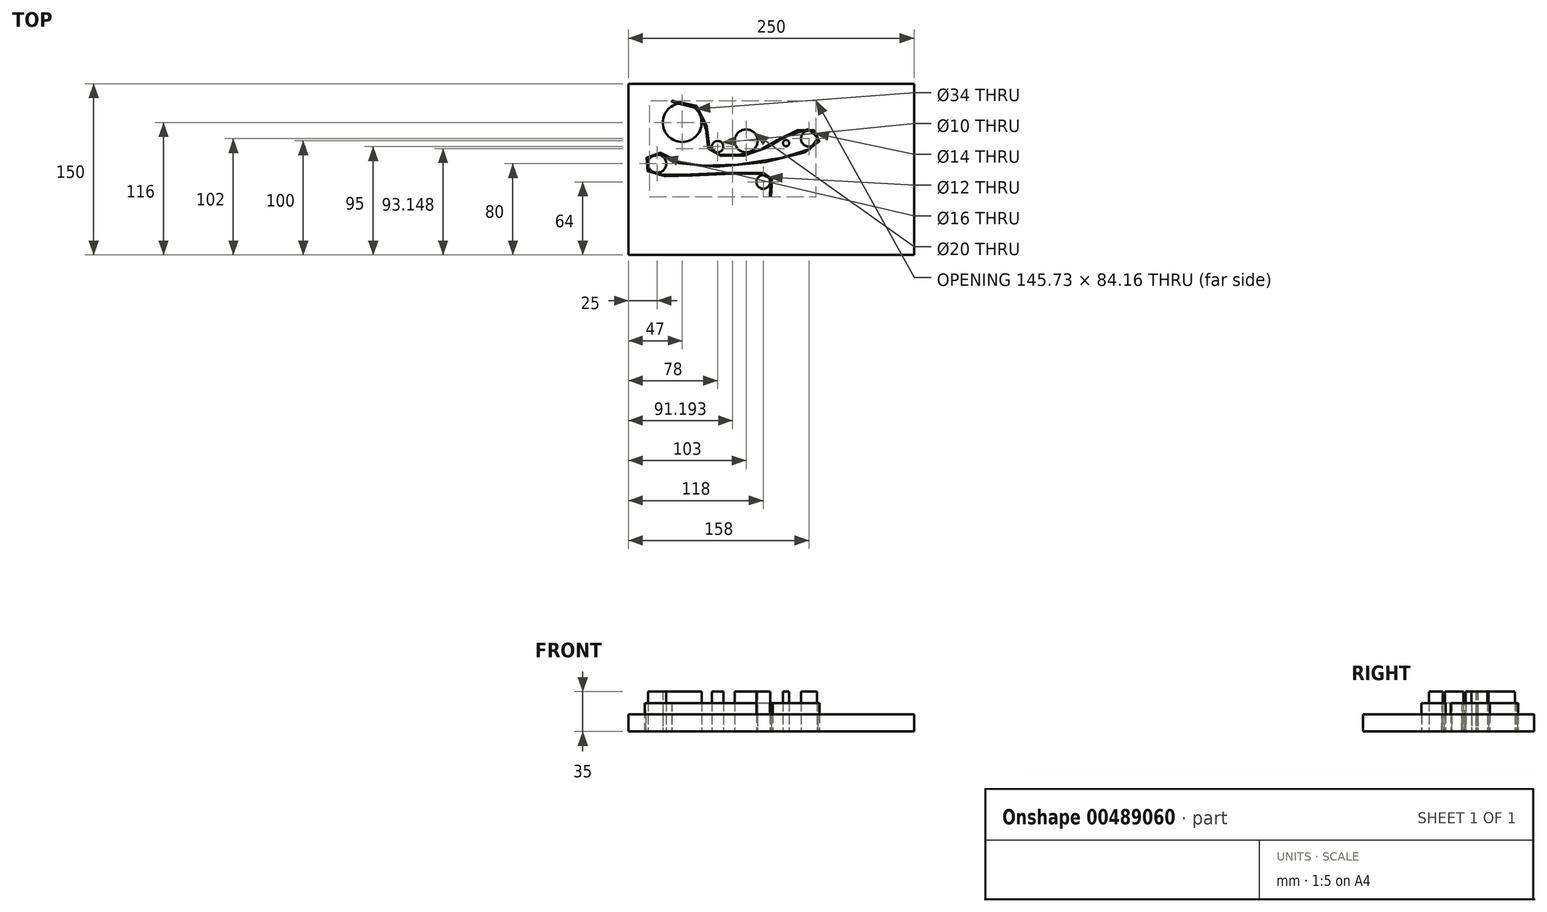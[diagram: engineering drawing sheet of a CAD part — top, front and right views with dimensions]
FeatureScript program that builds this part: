
annotation { "Feature Type Name" : "Feature", "Feature Type Description" : "" }
export const myFeature = defineFeature(function(context is Context, id is Id, definition is map)
    precondition{}
    {
        {
            var Q0;
            Q0=qCreatedBy(makeId("Top.planeOp"),FACE);
            var sketch = newSketch(context, id + "F0", { "sketchPlane" : qUnion([Q0])});
            skLineSegment(sketch, "E0.bottom", {"start": v(-113, 112) * mm, "end": v(137, 112) * mm});
            skLineSegment(sketch, "E0.top", {"start": v(-113, -38) * mm, "end": v(137, -38) * mm});
            skLineSegment(sketch, "E0.left", {"start": v(-113, 112) * mm, "end": v(-113, -38) * mm});
            skLineSegment(sketch, "E0.right", {"start": v(137, 112) * mm, "end": v(137, -38) * mm});
            skCircle(sketch, "E1", {"center": v(-66, 78) * mm, "radius": 17 * mm});
            skCircle(sketch, "E2", {"center": v(-35, 57) * mm, "radius": 5 * mm});
            skCircle(sketch, "E3", {"center": v(-10, 62) * mm, "radius": 10 * mm});
            skCircle(sketch, "E4", {"center": v(45, 64) * mm, "radius": 7 * mm});
            skCircle(sketch, "E5", {"center": v(25, 60) * mm, "radius": 2.75 * mm});
            skCircle(sketch, "E6", {"center": v(5, 26) * mm, "radius": 6 * mm});
            skCircle(sketch, "E7", {"center": v(-88, 42) * mm, "radius": 8 * mm});
            skLineSegment(sketch, "E8", {"start": v(-35, 62) * mm, "end": v(-14, 71.17) * mm});
            skLineSegment(sketch, "E9", {"start": v(-35, 52) * mm, "end": v(-10, 52) * mm});
            skFitSpline(sketch, "E10", {"points": [v(-75.22, 97.23) * mm, v(-45.88, 80.85) * mm, v(-41.4, 53.92) * mm, v(-30.29, 49.78) * mm, v(-3.76, 51.88) * mm, v(21.1, 64.78) * mm, v(47.28, 72.74) * mm, v(53.96, 64.44) * mm, v(47.46, 54.45) * mm, v(-64.37, 41.14) * mm, v(-88.04, 51.12) * mm, v(-97.25, 44.82) * mm, v(-95.52, 36.29) * mm, v(-81.1, 32.03) * mm, v(4.23, 34.03) * mm, v(12.06, 30.05) * mm, v(11.61, 13.07) * mm], "startDerivative": vector(662.98, 157.54) * mm, "endDerivative": vector(-153.55, -571.99) * mm});
            skFitSpline(sketch, "E11.0", {"points": [v(-75, 96.25) * mm, v(-71.63, 97.05) * mm, v(-65.54, 97.5) * mm, v(-58.23, 95.4) * mm, v(-53.51, 91.88) * mm, v(-50.52, 88.26) * mm, v(-48.68, 85.2) * mm, v(-47.23, 81.9) * mm, v(-46.18, 78.42) * mm, v(-45.47, 74.82) * mm, v(-45, 71.18) * mm, v(-44.7, 67.6) * mm, v(-44.47, 64.13) * mm, v(-44.2, 60.88) * mm, v(-43.87, 58.4) * mm, v(-43.49, 56.59) * mm, v(-43.13, 55.32) * mm, v(-42.67, 54.15) * mm, v(-42.1, 53.1) * mm, v(-41.4, 52.17) * mm, v(-40.31, 51.13) * mm, v(-38.72, 50.17) * mm, v(-36.55, 49.47) * mm, v(-34.15, 49.06) * mm, v(-31.98, 48.88) * mm, v(-30.15, 48.77) * mm, v(-28.24, 48.68) * mm, v(-25.74, 48.59) * mm, v(-21.53, 48.54) * mm, v(-15.98, 48.72) * mm, v(-10.35, 49.35) * mm, v(-5.96, 50.23) * mm, v(-2.76, 51.1) * mm, v(0.28, 52.18) * mm, v(4.2, 53.87) * mm, v(8.89, 56.37) * mm, v(13.57, 59.19) * mm, v(17.45, 61.52) * mm, v(19.97, 63) * mm, v(22.05, 64.17) * mm, v(24.19, 65.33) * mm, v(26.93, 66.75) * mm, v(30.28, 68.33) * mm, v(34.71, 70.19) * mm, v(38.98, 71.54) * mm, v(42.77, 72.14) * mm, v(44.87, 72.17) * mm, v(46.35, 71.96) * mm, v(47.35, 71.69) * mm, v(48.26, 71.3) * mm, v(49.36, 70.64) * mm, v(50.55, 69.58) * mm, v(51.67, 68) * mm, v(52.35, 66.55) * mm, v(52.74, 65.35) * mm, v(52.95, 64.45) * mm, v(53.09, 63.58) * mm, v(53.15, 62.46) * mm, v(53, 61.16) * mm, v(52.36, 59.66) * mm, v(51.13, 58.1) * mm, v(49.44, 56.76) * mm, v(47.64, 55.67) * mm, v(45.52, 54.56) * mm, v(42.26, 53.15) * mm, v(37.5, 51.47) * mm, v(32.01, 49.83) * mm, v(23.86, 47.73) * mm, v(12.34, 45.3) * mm, v(-2.78, 42.85) * mm, v(-18.38, 41.05) * mm, v(-31.13, 40.22) * mm, v(-40.76, 40.02) * mm, v(-47.6, 40.13) * mm, v(-53.97, 40.52) * mm, v(-58.77, 41.09) * mm, v(-62.27, 41.7) * mm, v(-64.7, 42.23) * mm, v(-66.95, 42.84) * mm, v(-69.7, 43.74) * mm, v(-72.76, 45) * mm, v(-75.9, 46.6) * mm, v(-78.62, 48.18) * mm, v(-81.04, 49.65) * mm, v(-83.3, 50.9) * mm, v(-85.13, 51.66) * mm, v(-86.64, 52.02) * mm, v(-87.8, 52.15) * mm, v(-89, 52.1) * mm, v(-90.57, 51.82) * mm, v(-92.47, 51.13) * mm, v(-94.57, 49.84) * mm, v(-96.08, 48.47) * mm, v(-97.08, 47.24) * mm, v(-97.7, 46.25) * mm, v(-98.2, 45.2) * mm, v(-98.53, 44.11) * mm, v(-98.7, 43.02) * mm, v(-98.74, 41.57) * mm, v(-98.47, 39.8) * mm, v(-97.73, 37.83) * mm, v(-96.68, 36.07) * mm, v(-95.4, 34.58) * mm, v(-93.84, 33.37) * mm, v(-91.93, 32.45) * mm, v(-89.63, 31.79) * mm, v(-86.83, 31.35) * mm, v(-84.02, 31.13) * mm, v(-81.42, 31.04) * mm, v(-78.57, 30.98) * mm, v(-74.57, 31) * mm, v(-69.16, 31.12) * mm, v(-63.27, 31.33) * mm, v(-54.89, 31.69) * mm, v(-43.73, 32.24) * mm, v(-30.14, 32.92) * mm, v(-19.38, 33.35) * mm, v(-11.57, 33.53) * mm, v(-6.22, 33.56) * mm, v(-2.27, 33.5) * mm, v(0.5, 33.36) * mm, v(2.4, 33.23) * mm, v(4.06, 33.06) * mm, v(5.5, 32.84) * mm, v(6.7, 32.6) * mm, v(8.06, 32.2) * mm, v(9.3, 31.65) * mm, v(10.11, 31.01) * mm, v(10.63, 30.42) * mm, v(10.97, 29.93) * mm, v(11.3, 29.36) * mm, v(11.6, 28.75) * mm, v(11.85, 28.1) * mm, v(12.14, 27.12) * mm, v(12.4, 25.68) * mm, v(12.47, 23.52) * mm, v(12.18, 19.91) * mm, v(11.44, 16.28) * mm, v(10.65, 13.33) * mm]});
            skLineSegment(sketch, "E12", {"start": v(-75.22, 97.23) * mm, "end": v(-75, 96.25) * mm});
            skLineSegment(sketch, "E13", {"start": v(11.61, 13.07) * mm, "end": v(10.69, 13.49) * mm});
            skSolve(sketch);
        }
        {
            var Q0;
            Q0=makeQuery(id+"F0.imprint","IMPRINT",FACE,{"disambiguationData":[TD([[makeQuery(id+"F0.imprint","IMPRINT",EDGE,{"derivedFrom":sQuery(id+"F0.wireOp",EDGE,"E7")}),1.0]])]});
            var Q1;
            Q1=makeQuery(id+"F0.imprint","IMPRINT",FACE,{"disambiguationData":[TD([[makeQuery(id+"F0.imprint","IMPRINT",EDGE,{"derivedFrom":sQuery(id+"F0.wireOp",EDGE,"E1")}),1.0]])]});
            var Q2;
            {var subQ0=sQuery(id+"F0.wireOp",EDGE,"E2");var subQ1=makeQuery(id+"F0.imprint","INTERSECT",VERTEX,{"derivedFrom":[subQ0,sQuery(id+"F0.wireOp",EDGE,"E8")]});Q2=makeQuery(id+"F0.imprint","IMPRINT",FACE,{"disambiguationData":[TD([[makeQuery(id+"F0.imprint","IMPRINT",EDGE,{"disambiguationData":[TD([[subQ1,-1.0]])],"derivedFrom":subQ0}),1.0]])]});}
            var Q3;
            {var subQ0=sQuery(id+"F0.wireOp",EDGE,"E3");var subQ1=makeQuery(id+"F0.imprint","INTERSECT",VERTEX,{"derivedFrom":[subQ0,sQuery(id+"F0.wireOp",EDGE,"E8")]});Q3=makeQuery(id+"F0.imprint","IMPRINT",FACE,{"disambiguationData":[TD([[makeQuery(id+"F0.imprint","IMPRINT",EDGE,{"disambiguationData":[TD([[subQ1,-1.0]])],"derivedFrom":subQ0}),1.0]])]});}
            var Q4;
            Q4=makeQuery(id+"F0.imprint","IMPRINT",FACE,{"disambiguationData":[TD([[makeQuery(id+"F0.imprint","IMPRINT",EDGE,{"derivedFrom":sQuery(id+"F0.wireOp",EDGE,"E6")}),1.0]])]});
            var Q5;
            Q5=makeQuery(id+"F0.imprint","IMPRINT",FACE,{"disambiguationData":[TD([[makeQuery(id+"F0.imprint","IMPRINT",EDGE,{"derivedFrom":sQuery(id+"F0.wireOp",EDGE,"E4")}),1.0]])]});
            var Q6;
            Q6=makeQuery(id+"F0.imprint","IMPRINT",FACE,{"disambiguationData":[TD([[makeQuery(id+"F0.imprint","IMPRINT",EDGE,{"derivedFrom":sQuery(id+"F0.wireOp",EDGE,"E5")}),1.0]])]});
            extrude(context, id + "F1", {"entities" : qUnion([Q0, Q1, Q2, Q3, Q4, Q5, Q6]), "depth" : 35 * mm});
        }
        {
            var Q0;
            Q0=makeQuery(id+"F0.imprint","IMPRINT",FACE,{"disambiguationData":[TD([[makeQuery(id+"F0.imprint","IMPRINT",EDGE,{"derivedFrom":sQuery(id+"F0.wireOp",EDGE,"E0.bottom")}),-1.0]])]});
            var Q1;
            {var subQ0=sQuery(id+"F0.wireOp",EDGE,"E8");Q1=makeQuery(id+"F0.imprint","IMPRINT",FACE,{"disambiguationData":[TD([[makeQuery(id+"F0.imprint","IMPRINT",EDGE,{"derivedFrom":subQ0}),-1.0]])]});}
            extrude(context, id + "F2", {"entities" : qUnion([Q0, Q1]), "depth" : 15 * mm});
        }
        {
            var Q0;
            Q0=makeQuery(id+"F0.imprint","IMPRINT",FACE,{"disambiguationData":[TD([[makeQuery(id+"F0.imprint","IMPRINT",EDGE,{"derivedFrom":sQuery(id+"F0.wireOp",EDGE,"E10")}),-1.0]])]});
            extrude(context, id + "F3", {"entities" : qUnion([Q0]), "depth" : 25 * mm});
        }
    });
